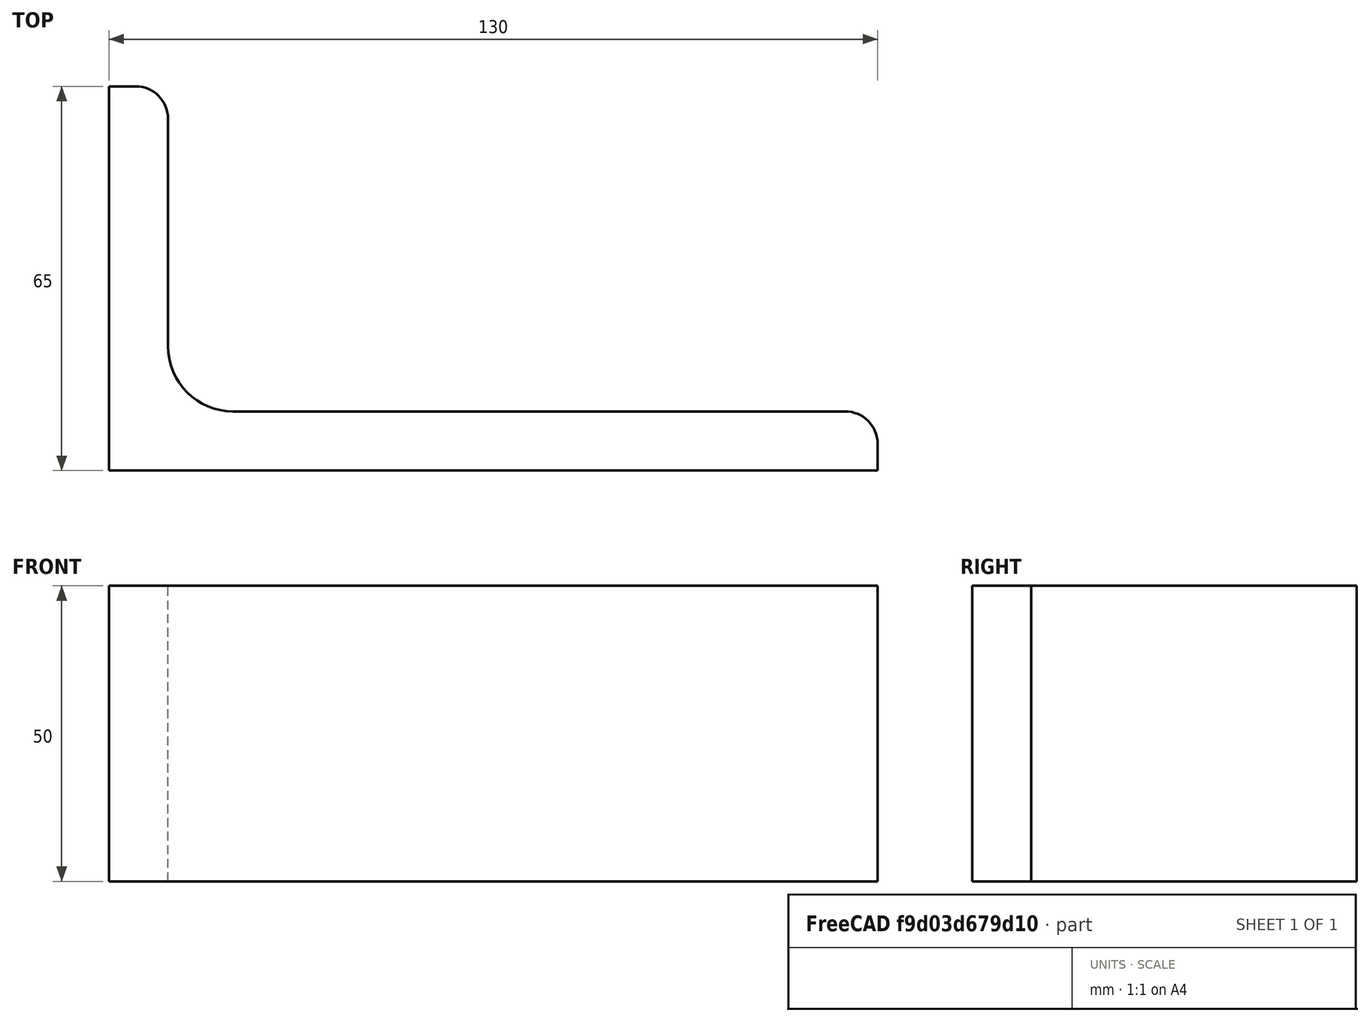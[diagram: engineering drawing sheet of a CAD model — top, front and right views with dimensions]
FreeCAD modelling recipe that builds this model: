
FCSTD DOCUMENT  (FreeCAD 0.15R4671 (Git))
Label: Angle Bar 130x65x10 EN10056 S235JR
License: All rights reserved
LicenseURL: http://en.wikipedia.org/wiki/All_rights_reserved
objects: Sketcher::SketchObject×1, Part::Extrusion×1
note: 2 computed .brp shape members not serialized (recipe doc carries the construction recipe); baked Part::Feature solids carry a one-line shape summary decoded from their .brp

FEATURE [Sketcher::SketchObject] Sketch
  sketch-geometry (9):
    g0: LineSegment StartX=0 StartY=0 StartZ=0 EndX=130 EndY=0 EndZ=0
    g1: LineSegment StartX=130 StartY=0 StartZ=0 EndX=130 EndY=4.5 EndZ=0
    g2: LineSegment StartX=124.5 StartY=10 StartZ=0 EndX=21 EndY=10 EndZ=0
    g3: LineSegment StartX=0 StartY=0 StartZ=0 EndX=0 EndY=65 EndZ=0
    g4: LineSegment StartX=0 StartY=65 StartZ=0 EndX=4.5 EndY=65 EndZ=0
    g5: LineSegment StartX=10 StartY=59.5 StartZ=0 EndX=10 EndY=21 EndZ=0
    g6: ArcOfCircle CenterX=21 CenterY=21 CenterZ=0 NormalX=0 NormalY=0 NormalZ=1 Radius=11 StartAngle=3.14159 EndAngle=4.71239
    g7: ArcOfCircle CenterX=4.5 CenterY=59.5 CenterZ=0 NormalX=0 NormalY=0 NormalZ=1 Radius=5.5 StartAngle=0 EndAngle=1.5708
    g8: ArcOfCircle CenterX=124.5 CenterY=4.5 CenterZ=0 NormalX=0 NormalY=0 NormalZ=1 Radius=5.5 StartAngle=0 EndAngle=1.5708
  constraints (23):
    c: Coincident(g0,g-1)
    c: Horizontal(g0)
    c: Coincident(g1,g0)
    c: Vertical(g1)
    c: Horizontal(g2)
    c: Coincident(g3,g-1)
    c: Vertical(g3)
    c: Coincident(g4,g3)
    c: Horizontal(g4)
    c: Vertical(g5)
    c: Tangent(g5,g6) = -1.5708
    c: Tangent(g2,g6) = 1.5708
    c: Tangent(g4,g7) = 1.5708
    c: Tangent(g5,g7) = 1.5708
    c: Tangent(g2,g8) = -1.5708
    c: Tangent(g1,g8) = -1.5708
    c: DistanceX(g0) = 130
    c: DistanceY(g3) = 65
    c: DistanceY(g0,g2) = 10
    c: DistanceX(g3,g5) = 10
    c: Radius(g6) = 11
    c: Radius(g8) = 5.5
    c: Radius(g7) = 5.5
FEATURE [Part::Extrusion] Extrude  label="Angle Bar 130x65x10 EN10056 S235JR"
  Base = -> Sketch
  Dir = (0,0,50)
  Solid = true
